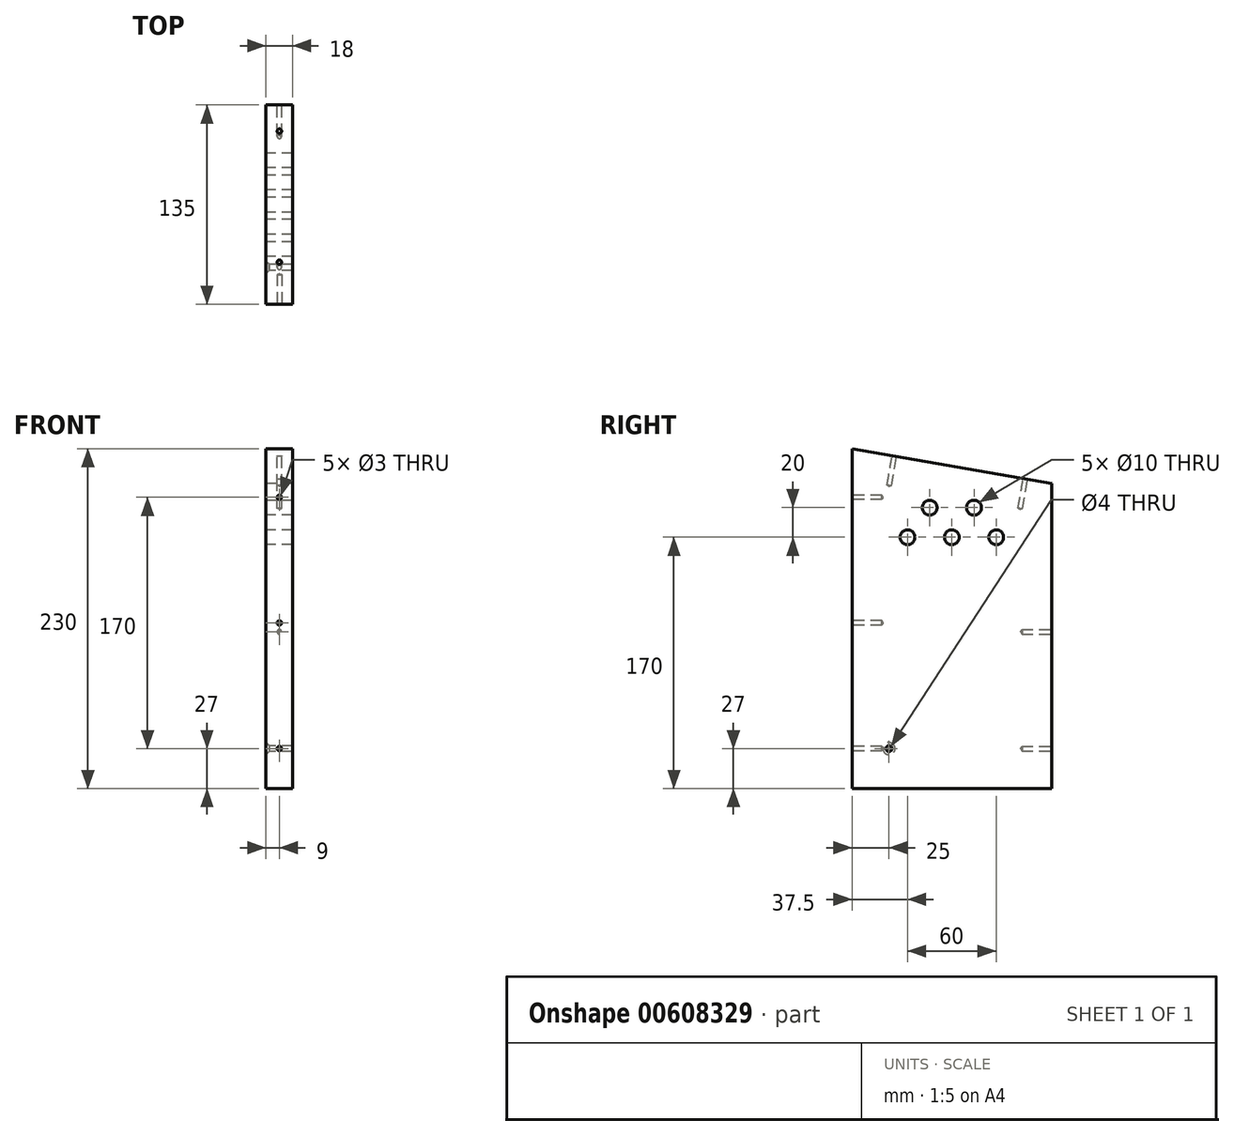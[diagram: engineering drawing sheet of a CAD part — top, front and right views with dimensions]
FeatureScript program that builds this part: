
annotation { "Feature Type Name" : "Feature", "Feature Type Description" : "" }
export const myFeature = defineFeature(function(context is Context, id is Id, definition is map)
    precondition{}
    {
        {
            var Q0;
            Q0=qCreatedBy(makeId("Right.planeOp"),FACE);
            var sketch = newSketch(context, id + "F0", { "sketchPlane" : qUnion([Q0])});
            skLineSegment(sketch, "E0", {"start": v(0, 0) * mm, "end": v(0, 230) * mm});
            skLineSegment(sketch, "E1", {"start": v(0, 230) * mm, "end": v(135, 206.2) * mm});
            skLineSegment(sketch, "E2", {"start": v(135, 206.2) * mm, "end": v(135, 0) * mm});
            skLineSegment(sketch, "E3", {"start": v(135, 0) * mm, "end": v(0, 0) * mm});
            skPoint(sketch, "E4", {"position": v(67.5, 170) * mm});
            skPoint(sketch, "E5", {"position": v(37.5, 170) * mm});
            skPoint(sketch, "E6", {"position": v(97.5, 170) * mm});
            skPoint(sketch, "E7", {"position": v(52.5, 190) * mm});
            skPoint(sketch, "E8", {"position": v(82.5, 190) * mm});
            skPoint(sketch, "E9", {"position": v(25, 27) * mm});
            skPoint(sketch, "E10", {"position": v(67.5, 0) * mm});
            skSolve(sketch);
        }
        {
            var Q0;
            Q0=makeQuery(id+"F0.imprint","IMPRINT",FACE,{"disambiguationData":[TD([[makeQuery(id+"F0.imprint","IMPRINT",EDGE,{"derivedFrom":sQuery(id+"F0.wireOp",EDGE,"E0")}),-1.0]])]});
            extrude(context, id + "F1", {"entities" : qUnion([Q0]), "depth" : 18 * mm, "offsetDistance" : 25 * mm});
        }
        {
            var Q0;
            Q0=sQuery(id+"F0.wireOp",VERTEX,"E5");
            var Q1;
            Q1=sQuery(id+"F0.wireOp",VERTEX,"E4");
            var Q2;
            Q2=sQuery(id+"F0.wireOp",VERTEX,"E6");
            var Q3;
            Q3=makeQuery(id+"F1.opExtrude","SWEPT_BODY",BODY,{"disambiguationData":[OSD([sQuery(id+"F0.wireOp",EDGE,"E0"),sQuery(id+"F0.wireOp",EDGE,"E1"),sQuery(id+"F0.wireOp",EDGE,"E2"),sQuery(id+"F0.wireOp",EDGE,"E3")])]});
            hole(context, id + "F2", {"style" : HoleStyle.SIMPLE, "endStyle" : HoleEndStyle.THROUGH, "oppositeDirection" : true, "holeDiameter" : 10 * mm, "majorDiameter" : 5 * mm, "isTappedThrough" : true, "tappedDepth" : 12 * mm, "tapClearance" : 3, "locations" : qUnion([Q0, Q1, Q2]), "scope" : qUnion([Q3])});
        }
        {
            var Q0;
            Q0=sQuery(id+"F0.wireOp",VERTEX,"E7");
            var Q1;
            Q1=sQuery(id+"F0.wireOp",VERTEX,"E8");
            var Q2;
            Q2=makeQuery(id+"F1.opExtrude","SWEPT_BODY",BODY,{"disambiguationData":[OSD([sQuery(id+"F0.wireOp",EDGE,"E0"),sQuery(id+"F0.wireOp",EDGE,"E1"),sQuery(id+"F0.wireOp",EDGE,"E2"),sQuery(id+"F0.wireOp",EDGE,"E3")])]});
            hole(context, id + "F3", {"style" : HoleStyle.SIMPLE, "endStyle" : HoleEndStyle.THROUGH, "oppositeDirection" : true, "holeDiameter" : 10 * mm, "majorDiameter" : 5 * mm, "isTappedThrough" : true, "tappedDepth" : 12 * mm, "tapClearance" : 3, "locations" : qUnion([Q0, Q1]), "scope" : qUnion([Q2])});
        }
        {
            var Q0;
            Q0=sQuery(id+"F0.wireOp",VERTEX,"E9");
            var Q1;
            Q1=makeQuery(id+"F1.opExtrude","SWEPT_BODY",BODY,{"disambiguationData":[OSD([sQuery(id+"F0.wireOp",EDGE,"E0"),sQuery(id+"F0.wireOp",EDGE,"E1"),sQuery(id+"F0.wireOp",EDGE,"E2"),sQuery(id+"F0.wireOp",EDGE,"E3")])]});
            hole(context, id + "F4", {"style" : HoleStyle.C_SINK, "endStyle" : HoleEndStyle.THROUGH, "oppositeDirection" : true, "holeDiameter" : 4 * mm, "cSinkDiameter" : 8.2 * mm, "cSinkAngle" : 90 * degree, "majorDiameter" : 5 * mm, "isTappedThrough" : true, "tappedDepth" : 12 * mm, "tapClearance" : 3, "locations" : qUnion([Q0]), "scope" : qUnion([Q1])});
        }
        {
            var Q0;
            Q0=makeQuery(id+"F1.opExtrude","SWEPT_FACE",FACE,{"disambiguationData":[OSD([sQuery(id+"F0.wireOp",EDGE,"E2")])]});
            var sketch = newSketch(context, id + "F5", { "sketchPlane" : qUnion([Q0])});
            skPoint(sketch, "E11", {"position": v(-9, 27) * mm});
            skPoint(sketch, "E11.positionSnap0", {"position": v(-9, 0) * mm});
            skPoint(sketch, "E12", {"position": v(-9, 106) * mm});
            skSolve(sketch);
        }
        {
            var Q0;
            Q0=sQuery(id+"F5.wireOp",VERTEX,"E11");
            var Q1;
            Q1=sQuery(id+"F5.wireOp",VERTEX,"E12");
            var Q2;
            Q2=sQuery(id+"F5.wireOp",VERTEX,"8858b236-943e-4bb1-8c07-c0e3087772b6");
            var Q3;
            Q3=makeQuery(id+"F1.opExtrude","SWEPT_BODY",BODY,{"disambiguationData":[OSD([sQuery(id+"F0.wireOp",EDGE,"E0"),sQuery(id+"F0.wireOp",EDGE,"E1"),sQuery(id+"F0.wireOp",EDGE,"E2"),sQuery(id+"F0.wireOp",EDGE,"E3")])]});
            hole(context, id + "F6", {"style" : HoleStyle.SIMPLE, "endStyle" : HoleEndStyle.BLIND, "holeDiameter" : 3 * mm, "majorDiameter" : 5 * mm, "holeDepth" : 20 * mm, "isTappedThrough" : true, "tappedDepth" : 12 * mm, "tapClearance" : 3, "locations" : qUnion([Q0, Q1, Q2]), "scope" : qUnion([Q3])});
        }
        {
            var Q0;
            Q0=makeQuery(id+"F1.opExtrude","SWEPT_FACE",FACE,{"disambiguationData":[OSD([sQuery(id+"F0.wireOp",EDGE,"E0")])]});
            var sketch = newSketch(context, id + "F7", { "sketchPlane" : qUnion([Q0])});
            skPoint(sketch, "E13", {"position": v(9, 27) * mm});
            skPoint(sketch, "E13.positionSnap0", {"position": v(9, 0) * mm});
            skPoint(sketch, "E14", {"position": v(9, 112) * mm});
            skPoint(sketch, "E15", {"position": v(9, 197) * mm});
            skSolve(sketch);
        }
        {
            var Q0;
            Q0=sQuery(id+"F7.wireOp",VERTEX,"E13");
            var Q1;
            Q1=sQuery(id+"F7.wireOp",VERTEX,"E14");
            var Q2;
            Q2=sQuery(id+"F7.wireOp",VERTEX,"E15");
            var Q3;
            Q3=makeQuery(id+"F1.opExtrude","SWEPT_BODY",BODY,{"disambiguationData":[OSD([sQuery(id+"F0.wireOp",EDGE,"E0"),sQuery(id+"F0.wireOp",EDGE,"E1"),sQuery(id+"F0.wireOp",EDGE,"E2"),sQuery(id+"F0.wireOp",EDGE,"E3")])]});
            hole(context, id + "F8", {"style" : HoleStyle.SIMPLE, "endStyle" : HoleEndStyle.BLIND, "holeDiameter" : 3 * mm, "majorDiameter" : 5 * mm, "holeDepth" : 20 * mm, "isTappedThrough" : true, "tappedDepth" : 12 * mm, "tapClearance" : 3, "locations" : qUnion([Q0, Q1, Q2]), "scope" : qUnion([Q3])});
        }
        {
            var Q0;
            Q0=makeQuery(id+"F1.opExtrude","SWEPT_FACE",FACE,{"disambiguationData":[OSD([sQuery(id+"F0.wireOp",EDGE,"E1")])]});
            var sketch = newSketch(context, id + "F9", { "sketchPlane" : qUnion([Q0])});
            skPoint(sketch, "E16", {"position": v(9, 79.14) * mm});
            skPoint(sketch, "E16.positionSnap0", {"position": v(9, 97.14) * mm});
            skPoint(sketch, "E17", {"position": v(9, -10.86) * mm});
            skSolve(sketch);
        }
        {
            var Q0;
            Q0=sQuery(id+"F9.wireOp",VERTEX,"E17");
            var Q1;
            Q1=sQuery(id+"F9.wireOp",VERTEX,"E16");
            var Q2;
            Q2=makeQuery(id+"F1.opExtrude","SWEPT_BODY",BODY,{"disambiguationData":[OSD([sQuery(id+"F0.wireOp",EDGE,"E0"),sQuery(id+"F0.wireOp",EDGE,"E1"),sQuery(id+"F0.wireOp",EDGE,"E2"),sQuery(id+"F0.wireOp",EDGE,"E3")])]});
            hole(context, id + "F10", {"style" : HoleStyle.SIMPLE, "endStyle" : HoleEndStyle.BLIND, "holeDiameter" : 3 * mm, "majorDiameter" : 5 * mm, "holeDepth" : 20 * mm, "isTappedThrough" : true, "tappedDepth" : 12 * mm, "tapClearance" : 3, "locations" : qUnion([Q0, Q1]), "scope" : qUnion([Q2])});
        }
    });
